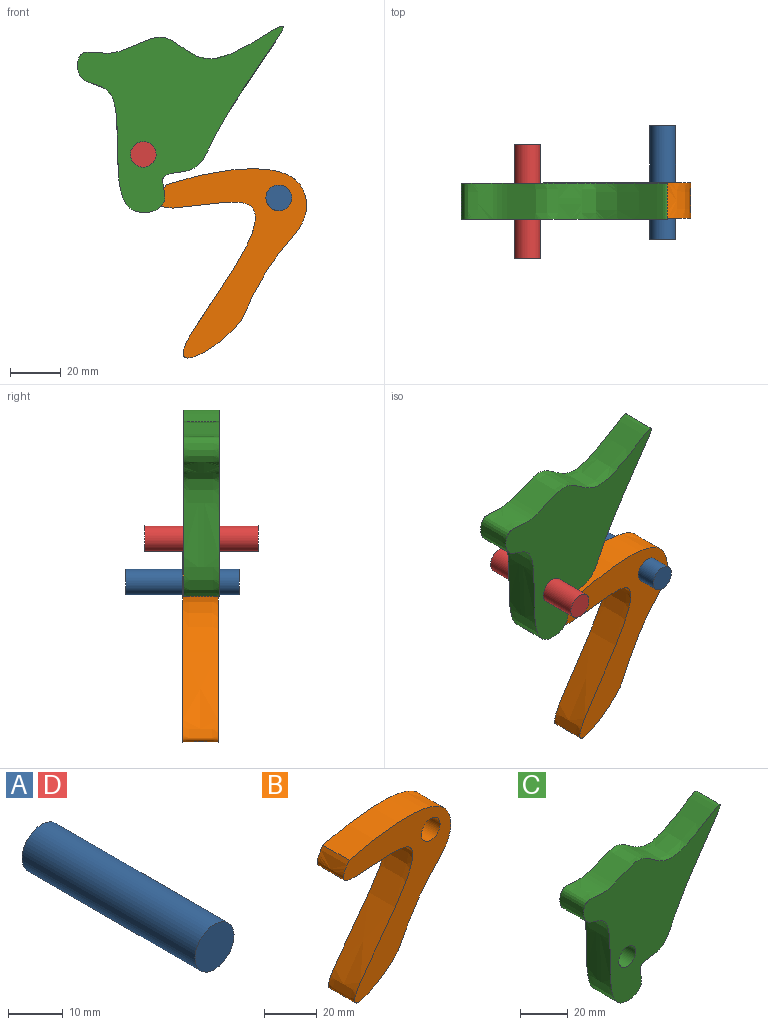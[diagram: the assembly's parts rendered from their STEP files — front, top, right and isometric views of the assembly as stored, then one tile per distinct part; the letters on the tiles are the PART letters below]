
ASSEMBLY  parts=4 mates=2
PART A: 3 faces, bbox 10.1x44.8x10.1 mm
  f0: cylinder r=5.05mm len=44.75mm, axis (0,1,0), area 1419.5mm2, adj f1,f2
  f1: plane 10.1x10.1mm, normal (0,-1,0), area 80.1mm2, adj f0
  f2: plane 10.1x10.1mm, normal (0,1,0), area 80.1mm2, adj f0
PART B: 5 faces, bbox 60.9x14.1x76.2 mm
  f0: extruded ~59.9x54.72mm, area 1644.5mm2, adj f1,f2,f3
  f1: extruded ~68.58x37.11mm, area 1968.6mm2, adj f0,f2,f3
  f2: plane 76.21x60.88mm, normal (0,-1,0), area 1503.2mm2, adj f0,f1,f4
  f3: plane 76.21x60.88mm, normal (0,1,0), area 1503.2mm2, adj f0,f1,f4
  f4: cylinder r=5.05mm len=14.07mm, axis (0,-1,0), area 446.3mm2, adj f2,f3
PART C: 4 faces, bbox 84.2x14.1x78.7 mm
  f0: extruded ~81.05x73.13mm, area 3637.1mm2, adj f1,f2
  f1: plane 84.15x78.65mm, normal (0,-1,0), area 2613mm2, adj f0,f3
  f2: plane 84.15x78.65mm, normal (0,1,0), area 2613mm2, adj f0,f3
  f3: cylinder r=5.05mm len=14.07mm, axis (0,-1,0), area 446.3mm2, adj f1,f2
PART D: same geometry as A
PLACE A t=(53.37,7.44,-17.1)mm
PLACE B rot(axis=(0,-1,0),3.1deg) t=(-44.6,-14.94,-25.59)mm
PLACE C t=(-33.84,-15.34,-26.08)mm
PLACE D at identity
MATE revolute C.f3 <-> D.f0  axis (0,-1,0) through (-41.8,-22.38,-31.12)mm
MATE revolute B.f4 <-> A.f0  axis (0,1,0) through (11.58,-14.94,-48.23)mm
